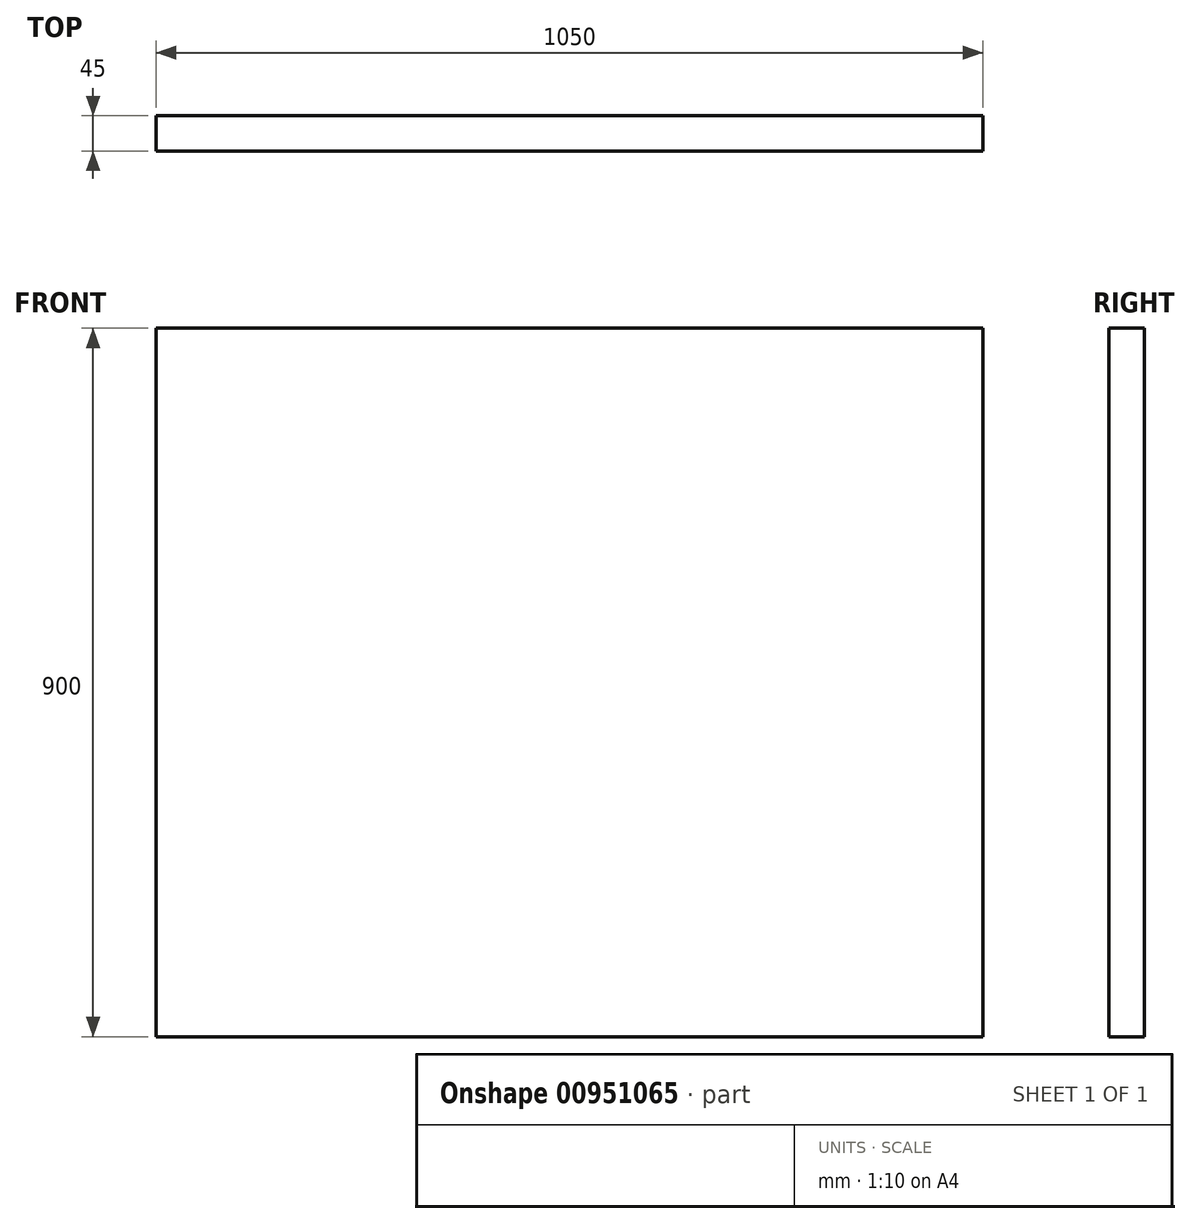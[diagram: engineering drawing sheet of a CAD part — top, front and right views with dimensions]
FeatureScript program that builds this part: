
annotation { "Feature Type Name" : "Feature", "Feature Type Description" : "" }
export const myFeature = defineFeature(function(context is Context, id is Id, definition is map)
    precondition{}
    {
        {
            var Q0;
            Q0=qCreatedBy(makeId("Front.planeOp"),FACE);
            var sketch = newSketch(context, id + "F0", { "sketchPlane" : qUnion([Q0])});
            skLineSegment(sketch, "E0.bottom", {"start": v(525, 431.68) * mm, "end": v(-525, 431.68) * mm});
            skLineSegment(sketch, "E0.top", {"start": v(525, -468.32) * mm, "end": v(-525, -468.32) * mm});
            skLineSegment(sketch, "E0.left", {"start": v(525, 431.68) * mm, "end": v(525, -468.32) * mm});
            skLineSegment(sketch, "E0.right", {"start": v(-525, 431.68) * mm, "end": v(-525, -468.32) * mm});
            skPoint(sketch, "E0.middle", {"position": v(0, -18.32) * mm});
            skSolve(sketch);
        }
        {
            var Q0;
            Q0 = qSketchRegion(id + "F0", true);
            extrude(context, id + "F1", {"entities" : qUnion([Q0]), "endBound" : BoundingType.SYMMETRIC, "depth" : 45 * mm, "offsetDistance" : 25 * mm});
        }
    });
